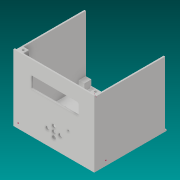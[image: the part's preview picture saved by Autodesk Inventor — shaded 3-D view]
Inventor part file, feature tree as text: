
AUTODESK INVENTOR PART (.ipt)
format: ipt  version: 2019 (Build 230136000, 136)  size: 998,400 bytes
history: native  units: mm
features: sketch x30, extrude x17, delete_face x8, other x8, hole x6, fillet x3, boolean_combine x1
ambient origin geometry x8: Origin, YZ Plane, XZ Plane, XY Plane, X Axis, Y Axis, Z Axis, Center Point
bodies: Solid1 (feature_tree), Solid2 (feature_tree), Solid3 (feature_tree), Solid4 (feature_tree), Solid5 (feature_tree), Solid6 (feature_tree), Solid137 (feature_tree), Solid139 (feature_tree), Solid141 (feature_tree), Solid142 (feature_tree)
feature tree (73):
  extrude  "Extrusion1"  Depth=5.0mm
  fillet  "Fillet1"  Radius=5.0mm
  delete_face  "Delete Face1"
  delete_face  "Delete Face2"
  delete_face  "Delete Face3"
  delete_face  "Delete Face4"
  delete_face  "Delete Face5"
  sketch  "Sketch2"  dims[d3=5.0mm d4=5.0mm]
  sketch  "Sketch3"  dims[d5=2.5mm d12=2.0mm d13=0.0mm d14=0.5mm]
  extrude  "Extrusion2"  Depth=5.0mm
  hole  "Hole1"  [1 undecoded]
  boolean_combine  "Combine1"
  fillet  "Fillet2"  Radius=0.5mm
  extrude  "Extrusion3"  Depth=2.0mm
  extrude  "Extrusion4"  TaperAngle=0.0deg  [1 undecoded]
  sketch  "Sketch8"  dims[d31=2.1mm d32=2.0mm]
  sketch  "Sketch9"  dims[d33=2.0mm d34=0.0mm d35=100.0mm]
  extrude  "Extrusion5"  Depth=2.0mm
  extrude  "Extrusion6"  Depth=2.0mm TaperAngle=0.0deg
  extrude  "Extrusion7"  Depth=2.0mm
  extrude  "Extrusion8"  Depth=100.0mm
  extrude  "Extrusion9"  Depth=2.0mm
  extrude  "Extrusion10"  Depth=2.0mm TaperAngle=0.0deg
  hole  "Hole2"  [1 undecoded]
  delete_face  "Delete Face6"
  delete_face  "Delete Face7"
  delete_face  "Delete Face39"
  sketch  "Sketch17"  dims[d63=3.2mm d64=6.0mm d65=4.0mm d66=2.0mm d67=90.0deg d68=4.0mm d69=0.0mm d70=10.0mm]
  extrude  "Extrusion11"  Depth=10.0mm
  hole  "Hole3"  [1 undecoded]
  extrude  "Extrusion12"  Depth=10.0mm
  extrude  "Extrusion13"  Depth=10.0mm TaperAngle=0.0deg
  hole  "Hole4"  [1 undecoded]
  hole  "Hole5"  [1 undecoded]
  extrude  "Extrusion14"  Depth=10.0mm
  sketch  "Sketch25"  dims[d109=9.5mm d110=9.5mm]
  extrude  "Extrusion15"  Depth=8.0mm
  fillet  "Fillet3"  Radius=1.5mm
  hole  "Hole6"  [1 undecoded]
  sketch  "Sketch28"  dims[d114=5.5mm]
  extrude  "Extrusion16"  Depth=10.0mm
  extrude  "Extrusion17"  Depth=9.5mm
  sketch  "Sketch1"  dims[d0=5.0mm d1=5.0mm d2=5.0mm]
  sketch  "Sketch4"  dims[d15=2.0mm d16=2.0mm]
  sketch  "Sketch5"  dims[d17=2.0mm d18=0.0mm d19=0.0mm]
  sketch  "Sketch6"  dims[d20=3.2mm d21=6.0mm d22=4.0mm d23=2.0mm d24=90.0deg d25=4.0mm d26=0.0mm d27=2.0mm]
  sketch  "Sketch7"  dims[d28=2.0mm d29=2.0mm d30=0.0mm]
  sketch  "Sketch10"  dims[d36=2.0mm d37=0.0mm d38=2.0mm]
  sketch  "Sketch11"  dims[d39=2.0mm d40=2.0mm d41=0.0mm]
  sketch  "Sketch12"  dims[d42=2.0mm d43=0.0mm d44=2.0mm d45=0.0mm]
  sketch  "Sketch13"  dims[d46=10.0mm d47=10.0mm]
  sketch  "Sketch14"  dims[d48=10.0mm d49=0.0mm d50=2.0mm d51=0.0mm]
  sketch  "Sketch15"  dims[d52=3.2mm d53=6.0mm d54=4.0mm d55=2.0mm d56=90.0deg d57=4.0mm d58=0.0mm d59=10.0mm]
  sketch  "Sketch16"  dims[d60=10.0mm d61=10.0mm d62=0.0mm]
  sketch  "Sketch18"  dims[d71=10.0mm d72=10.0mm d73=0.0mm]
  sketch  "Sketch19"  dims[d74=10.0mm d75=10.0mm]
  sketch  "Sketch20"  dims[d76=10.0mm d77=0.0mm]
  sketch  "Sketch21"  dims[d78=3.2mm d79=6.0mm d80=4.0mm d81=2.0mm d82=90.0deg d83=4.0mm d84=0.0mm d85=8.0mm]
  sketch  "Sketch22"  dims[d86=3.2mm d87=6.0mm d88=4.0mm d89=2.0mm d90=90.0deg d91=4.0mm d92=0.0mm d97=1.5mm]
  sketch  "Sketch23"  dims[d100=5.0mm d105=5.0mm]
  sketch  "Sketch24"  dims[d106=10.0mm d107=0.0mm d108=9.5mm]
  sketch  "Sketch26"  dims[d111=10.0mm d112=0.0mm]
  sketch  "Sketch27"  dims[d113=2.0mm]
  sketch  "Sketch29"  dims[d115=5.5mm]
  sketch  "Sketch30"  dims[d116=5.5mm d117=3.2mm d118=6.0mm d119=4.0mm d120=2.0mm d121=90.0deg d122=4.0mm d123=0.0mm d143=10.0mm d144=0.0mm d145=10.0mm d146=0.0mm]
  other  "Open CASCADE STEP translator 6.8 1.1.1_1:1"
  other  "4301x60507x6_3:1"
  other  "4301x60507x6_5:1"
  other  "4301x60507x6_7:1"
  other  "4301x60507x6_9:1"
  other  "4301x60507x6_11:1"
  other  "RC1602B-BIW-CSV--3DModel-STEP-56544_70:28"
  other  "RC1602B-BIW-CSV--3DModel-STEP-56544_70:30"
note: 7 required parameter values undecoded (feature->parameter linkage not recoverable at this tier; creation-order binding heuristic only, values carry confidence <= 0.55)
